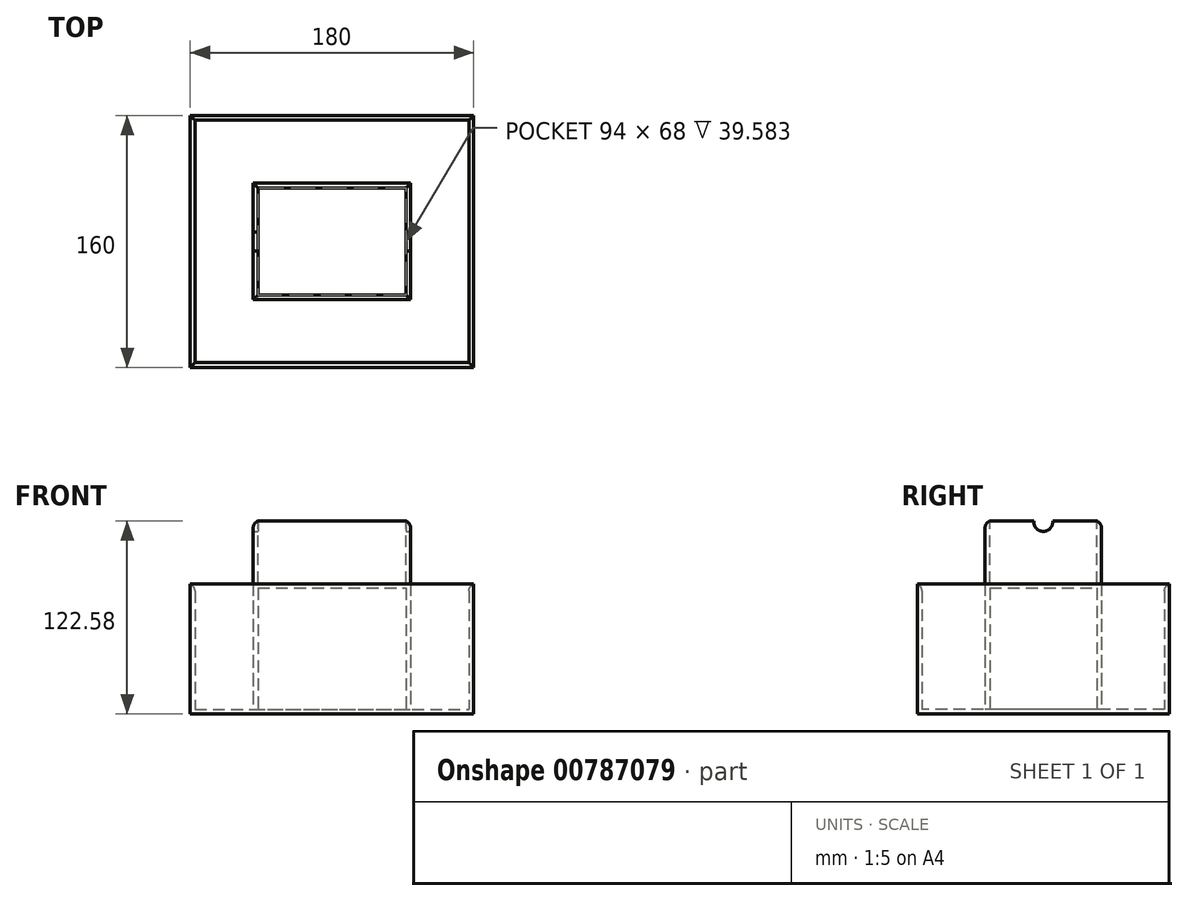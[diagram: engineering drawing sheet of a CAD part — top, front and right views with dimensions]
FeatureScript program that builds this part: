
annotation { "Feature Type Name" : "Feature", "Feature Type Description" : "" }
export const myFeature = defineFeature(function(context is Context, id is Id, definition is map)
    precondition{}
    {
        {
            var Q0;
            Q0=qCreatedBy(makeId("Top.planeOp"),FACE);
            var sketch = newSketch(context, id + "F0", { "sketchPlane" : qUnion([Q0])});
            skLineSegment(sketch, "E0.bottom", {"start": v(-130, 80) * mm, "end": v(50, 80) * mm});
            skLineSegment(sketch, "E0.top", {"start": v(-130, -80) * mm, "end": v(50, -80) * mm});
            skLineSegment(sketch, "E0.left", {"start": v(-130, 80) * mm, "end": v(-130, -80) * mm});
            skLineSegment(sketch, "E0.right", {"start": v(50, 80) * mm, "end": v(50, -80) * mm});
            skSolve(sketch);
        }
        {
            var Q0;
            Q0=qSketchRegion(id+"F0",true);
            extrude(context, id + "F1", {"entities" : qUnion([Q0]), "depth" : 1 * mm, "offsetDistance" : 25 * mm});
        }
        {
            var Q0;
            Q0=makeQuery(id+"F1.opExtrude","CAP_FACE",FACE,{"disambiguationData":[OSD([sQuery(id+"F0.wireOp",EDGE,"E0.bottom"),sQuery(id+"F0.wireOp",EDGE,"E0.top"),sQuery(id+"F0.wireOp",EDGE,"E0.left"),sQuery(id+"F0.wireOp",EDGE,"E0.right")])],"isStart":false});
            var sketch = newSketch(context, id + "F2", { "sketchPlane" : qUnion([Q0])});
            skLineSegment(sketch, "E1.bottom", {"start": v(-130, 80) * mm, "end": v(-120, 80) * mm});
            skLineSegment(sketch, "E1.top", {"start": v(-130, 70) * mm, "end": v(-120, 70) * mm});
            skLineSegment(sketch, "E1.left", {"start": v(-130, 80) * mm, "end": v(-130, 70) * mm});
            skLineSegment(sketch, "E1.right", {"start": v(-120, 80) * mm, "end": v(-120, 70) * mm});
            skLineSegment(sketch, "E2.bottom", {"start": v(50, 80) * mm, "end": v(40, 80) * mm});
            skLineSegment(sketch, "E2.top", {"start": v(50, 70) * mm, "end": v(40, 70) * mm});
            skLineSegment(sketch, "E2.left", {"start": v(50, 80) * mm, "end": v(50, 70) * mm});
            skLineSegment(sketch, "E2.right", {"start": v(40, 80) * mm, "end": v(40, 70) * mm});
            skLineSegment(sketch, "E3.bottom", {"start": v(-130, -80) * mm, "end": v(-120, -80) * mm});
            skLineSegment(sketch, "E3.top", {"start": v(-130, -70) * mm, "end": v(-120, -70) * mm});
            skLineSegment(sketch, "E3.left", {"start": v(-130, -80) * mm, "end": v(-130, -70) * mm});
            skLineSegment(sketch, "E3.right", {"start": v(-120, -80) * mm, "end": v(-120, -70) * mm});
            skLineSegment(sketch, "E4.bottom", {"start": v(50, -80) * mm, "end": v(40, -80) * mm});
            skLineSegment(sketch, "E4.top", {"start": v(50, -70) * mm, "end": v(40, -70) * mm});
            skLineSegment(sketch, "E4.left", {"start": v(50, -80) * mm, "end": v(50, -70) * mm});
            skLineSegment(sketch, "E4.right", {"start": v(40, -80) * mm, "end": v(40, -70) * mm});
            skSolve(sketch);
        }
        {
            var Q0;
            Q0=qSketchRegion(id+"F2",true);
            extrude(context, id + "F3", {"entities" : qUnion([Q0]), "operationType" : NewBodyOperationType.ADD, "depth" : 50 * mm, "offsetDistance" : 25 * mm});
        }
        {
            var Q0;
            Q0=makeQuery(id+"F1.opExtrude","CAP_FACE",FACE,{"disambiguationData":[OSD([sQuery(id+"F0.wireOp",EDGE,"E0.bottom"),sQuery(id+"F0.wireOp",EDGE,"E0.top"),sQuery(id+"F0.wireOp",EDGE,"E0.left"),sQuery(id+"F0.wireOp",EDGE,"E0.right")])],"isStart":true});
            shell(context, id + "F4", {"entities" : qUnion([Q0]), "thickness" : 1 * mm});
        }
        {
            var Q0;
            Q0=makeQuery(id+"F3.opExtrude","CAP_FACE",FACE,{"disambiguationData":[OSD([sQuery(id+"F2.wireOp",EDGE,"E3.bottom"),sQuery(id+"F2.wireOp",EDGE,"E3.top"),sQuery(id+"F2.wireOp",EDGE,"E3.left"),sQuery(id+"F2.wireOp",EDGE,"E3.right")])],"isStart":false});
            var sketch = newSketch(context, id + "F5", { "sketchPlane" : qUnion([Q0])});
            skLineSegment(sketch, "E5.bottom", {"start": v(-130, -80) * mm, "end": v(50, -80) * mm});
            skLineSegment(sketch, "E5.top", {"start": v(-130, 80) * mm, "end": v(50, 80) * mm});
            skLineSegment(sketch, "E5.left", {"start": v(-130, -80) * mm, "end": v(-130, 80) * mm});
            skLineSegment(sketch, "E5.right", {"start": v(50, -80) * mm, "end": v(50, 80) * mm});
            skSolve(sketch);
        }
        {
            var Q0;
            Q0=qSketchRegion(id+"F5",true);
            extrude(context, id + "F6", {"entities" : qUnion([Q0]), "operationType" : NewBodyOperationType.ADD, "depth" : 3 * mm, "offsetDistance" : 25 * mm});
        }
        {
            var Q0;
            Q0=makeQuery(id+"F6.opExtrude","CAP_FACE",FACE,{"disambiguationData":[OSD([sQuery(id+"F5.wireOp",EDGE,"E5.bottom"),sQuery(id+"F5.wireOp",EDGE,"E5.top"),sQuery(id+"F5.wireOp",EDGE,"E5.left"),sQuery(id+"F5.wireOp",EDGE,"E5.right")])],"isStart":false});
            var sketch = newSketch(context, id + "F7", { "sketchPlane" : qUnion([Q0])});
            skLineSegment(sketch, "E6.bottom", {"start": v(-130, 80) * mm, "end": v(50, 80) * mm});
            skLineSegment(sketch, "E6.top", {"start": v(-130, -80) * mm, "end": v(50, -80) * mm});
            skLineSegment(sketch, "E6.left", {"start": v(-130, 80) * mm, "end": v(-130, -80) * mm});
            skLineSegment(sketch, "E6.right", {"start": v(50, 80) * mm, "end": v(50, -80) * mm});
            skLineSegment(sketch, "E7.bottom", {"start": v(-127, 77) * mm, "end": v(47, 77) * mm});
            skLineSegment(sketch, "E7.top", {"start": v(-127, -77) * mm, "end": v(47, -77) * mm});
            skLineSegment(sketch, "E7.left", {"start": v(-127, 77) * mm, "end": v(-127, -77) * mm});
            skLineSegment(sketch, "E7.right", {"start": v(47, 77) * mm, "end": v(47, -77) * mm});
            skSolve(sketch);
        }
        {
            var Q0;
            Q0=qSketchRegion(id+"F7",true);
            extrude(context, id + "F8", {"entities" : qUnion([Q0]), "operationType" : NewBodyOperationType.ADD, "depth" : 80 * mm, "offsetDistance" : 25 * mm});
        }
        {
            var Q0;
            Q0=makeQuery(id+"F6.opExtrude","CAP_FACE",FACE,{"disambiguationData":[OSD([sQuery(id+"F5.wireOp",EDGE,"E5.bottom"),sQuery(id+"F5.wireOp",EDGE,"E5.top"),sQuery(id+"F5.wireOp",EDGE,"E5.left"),sQuery(id+"F5.wireOp",EDGE,"E5.right")])],"isStart":false});
            var sketch = newSketch(context, id + "F9", { "sketchPlane" : qUnion([Q0])});
            skLineSegment(sketch, "E8.bottom", {"start": v(-90, 37) * mm, "end": v(10, 37) * mm});
            skLineSegment(sketch, "E8.top", {"start": v(-90, -37) * mm, "end": v(10, -37) * mm});
            skLineSegment(sketch, "E8.left", {"start": v(-90, 37) * mm, "end": v(-90, -37) * mm});
            skLineSegment(sketch, "E8.right", {"start": v(10, 37) * mm, "end": v(10, -37) * mm});
            skSolve(sketch);
        }
        {
            var Q0;
            Q0=qSketchRegion(id+"F9",true);
            extrude(context, id + "F10", {"entities" : qUnion([Q0]), "operationType" : NewBodyOperationType.ADD, "depth" : 120 * mm, "offsetDistance" : 25 * mm});
        }
        {
            var Q0;
            Q0=makeQuery(id+"F10.opExtrude","CAP_FACE",FACE,{"disambiguationData":[OSD([sQuery(id+"F9.wireOp",EDGE,"E8.bottom"),sQuery(id+"F9.wireOp",EDGE,"E8.top"),sQuery(id+"F9.wireOp",EDGE,"E8.left"),sQuery(id+"F9.wireOp",EDGE,"E8.right")])],"isStart":false});
            var sketch = newSketch(context, id + "F11", { "sketchPlane" : qUnion([Q0])});
            skLineSegment(sketch, "E9.bottom", {"start": v(-87, 34) * mm, "end": v(7, 34) * mm});
            skLineSegment(sketch, "E9.top", {"start": v(-87, -34) * mm, "end": v(7, -34) * mm});
            skLineSegment(sketch, "E9.left", {"start": v(-87, 34) * mm, "end": v(-87, -34) * mm});
            skLineSegment(sketch, "E9.right", {"start": v(7, 34) * mm, "end": v(7, -34) * mm});
            skSolve(sketch);
        }
        {
            var Q0;
            Q0=qSketchRegion(id+"F11",true);
            extrude(context, id + "F12", {"entities" : qUnion([Q0]), "operationType" : NewBodyOperationType.REMOVE, "oppositeDirection" : true, "depth" : 40 * mm, "offsetDistance" : 25 * mm});
        }
        {
            var Q0;
            Q0=makeQuery(id+"F6.opExtrude","CAP_FACE",FACE,{"disambiguationData":[OSD([sQuery(id+"F5.wireOp",EDGE,"E5.bottom"),sQuery(id+"F5.wireOp",EDGE,"E5.top"),sQuery(id+"F5.wireOp",EDGE,"E5.left"),sQuery(id+"F5.wireOp",EDGE,"E5.right")])],"isStart":true});
            var sketch = newSketch(context, id + "F13", { "sketchPlane" : qUnion([Q0])});
            skLineSegment(sketch, "E10.bottom", {"start": v(-87, 34) * mm, "end": v(7, 34) * mm});
            skLineSegment(sketch, "E10.top", {"start": v(-87, -34) * mm, "end": v(7, -34) * mm});
            skLineSegment(sketch, "E10.left", {"start": v(-87, 34) * mm, "end": v(-87, -34) * mm});
            skLineSegment(sketch, "E10.right", {"start": v(7, 34) * mm, "end": v(7, -34) * mm});
            skSolve(sketch);
        }
        {
            var Q0;
            Q0=makeQuery(id+"F10.opExtrude","CAP_EDGE",EDGE,{"disambiguationData":[OSD([sQuery(id+"F9.wireOp",EDGE,"E8.top")])],"isStart":false});
            var Q1;
            Q1=makeQuery(id+"F10.opExtrude","CAP_EDGE",EDGE,{"disambiguationData":[OSD([sQuery(id+"F9.wireOp",EDGE,"E8.left")])],"isStart":false});
            var Q2;
            Q2=makeQuery(id+"F10.opExtrude","CAP_EDGE",EDGE,{"disambiguationData":[OSD([sQuery(id+"F9.wireOp",EDGE,"E8.bottom")])],"isStart":false});
            var Q3;
            Q3=makeQuery(id+"F10.opExtrude","CAP_EDGE",EDGE,{"disambiguationData":[OSD([sQuery(id+"F9.wireOp",EDGE,"E8.right")])],"isStart":false});
            var Q4;
            Q4=makeQuery(id+"F8.opExtrude","CAP_EDGE",EDGE,{"disambiguationData":[OSD([sQuery(id+"F7.wireOp",EDGE,"E7.top")])],"isStart":false});
            var Q5;
            Q5=makeQuery(id+"F8.opExtrude","CAP_EDGE",EDGE,{"disambiguationData":[OSD([sQuery(id+"F7.wireOp",EDGE,"E7.right")])],"isStart":false});
            var Q6;
            Q6=makeQuery(id+"F8.opExtrude","CAP_EDGE",EDGE,{"disambiguationData":[OSD([sQuery(id+"F7.wireOp",EDGE,"E7.left")])],"isStart":false});
            var Q7;
            Q7=makeQuery(id+"F8.opExtrude","CAP_EDGE",EDGE,{"disambiguationData":[OSD([sQuery(id+"F7.wireOp",EDGE,"E7.bottom")])],"isStart":false});
            fillet(context, id + "F14", {"entities" : qUnion([Q0, Q1, Q2, Q3, Q4, Q5, Q6, Q7]), "radius" : 5 * mm, "tangentPropagation" : true, "allowEdgeOverflow" : false});
        }
        {
            var Q0;
            Q0=makeQuery(id+"F10.opExtrude","SWEPT_FACE",FACE,{"disambiguationData":[OSD([sQuery(id+"F9.wireOp",EDGE,"E8.right")])]});
            var sketch = newSketch(context, id + "F15", { "sketchPlane" : qUnion([Q0])});
            skPoint(sketch, "E11.centerSnap0", {"position": v(0, 173) * mm});
            skCircle(sketch, "E12", {"center": v(0, 173) * mm, "radius": 6.03 * mm});
            skSolve(sketch);
        }
        {
            var Q0;
            Q0=qSketchRegion(id+"F15",true);
            extrude(context, id + "F16", {"entities" : qUnion([Q0]), "operationType" : NewBodyOperationType.REMOVE, "oppositeDirection" : true, "depth" : 500 * mm, "offsetDistance" : 25 * mm});
        }
        {
            var Q0;
            Q0=makeQuery(id+"F1.opExtrude","CAP_FACE",FACE,{"disambiguationData":[OSD([sQuery(id+"F0.wireOp",EDGE,"E0.bottom"),sQuery(id+"F0.wireOp",EDGE,"E0.top"),sQuery(id+"F0.wireOp",EDGE,"E0.left"),sQuery(id+"F0.wireOp",EDGE,"E0.right")])],"isStart":true});
            var sketch = newSketch(context, id + "F17", { "sketchPlane" : qUnion([Q0])});
            skLineSegment(sketch, "E13.bottom", {"start": v(-130, 80) * mm, "end": v(50, 80) * mm});
            skLineSegment(sketch, "E13.top", {"start": v(-130, -80) * mm, "end": v(50, -80) * mm});
            skLineSegment(sketch, "E13.left", {"start": v(-130, 80) * mm, "end": v(-130, -80) * mm});
            skLineSegment(sketch, "E13.right", {"start": v(50, 80) * mm, "end": v(50, -80) * mm});
            skSolve(sketch);
        }
        {
            var Q0;
            Q0=qSketchRegion(id+"F17",true);
            extrude(context, id + "F18", {"entities" : qUnion([Q0]), "operationType" : NewBodyOperationType.REMOVE, "oppositeDirection" : true, "depth" : 51 * mm, "offsetDistance" : 25 * mm});
        }
        {
            var Q0;
            Q0=makeQuery(id+"F13.imprint","IMPRINT",FACE,{"disambiguationData":[TD([[makeQuery(id+"F13.imprint","IMPRINT",EDGE,{"derivedFrom":sQuery(id+"F13.wireOp",EDGE,"E10.bottom")}),-1.0]])]});
            extrude(context, id + "F19", {"entities" : qUnion([Q0]), "operationType" : NewBodyOperationType.REMOVE, "oppositeDirection" : true, "depth" : 80 * mm, "offsetDistance" : 25 * mm});
        }
    });
